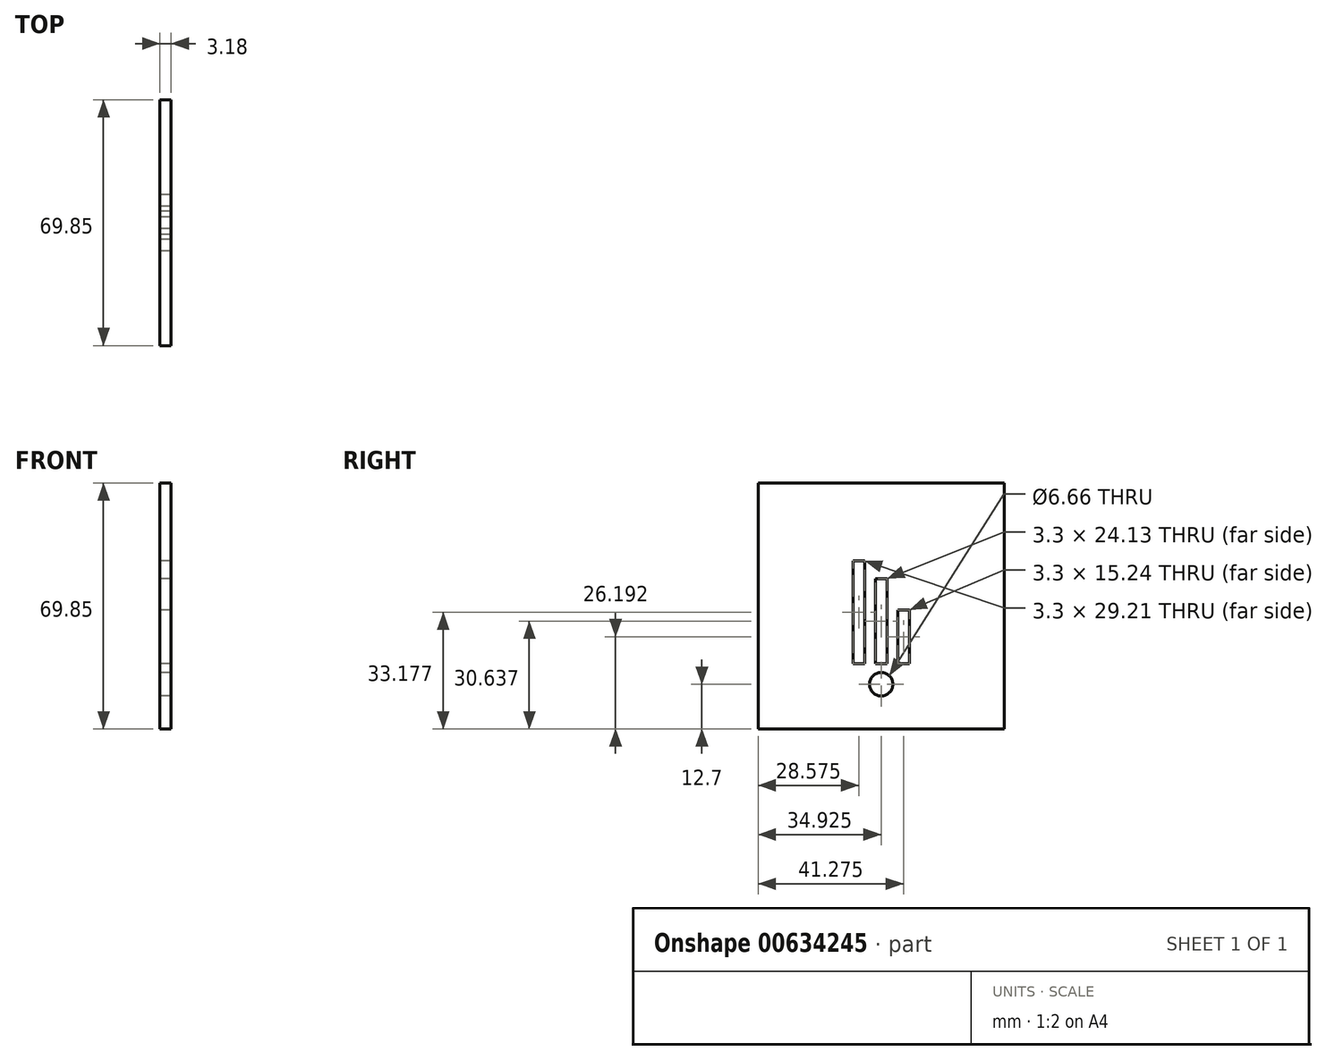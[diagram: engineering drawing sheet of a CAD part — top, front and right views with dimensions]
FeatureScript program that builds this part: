
annotation { "Feature Type Name" : "Feature", "Feature Type Description" : "" }
export const myFeature = defineFeature(function(context is Context, id is Id, definition is map)
    precondition{}
    {
        {
            var Q0;
            Q0=qCreatedBy(makeId("Right.planeOp"),FACE);
            var sketch = newSketch(context, id + "F0", { "sketchPlane" : qUnion([Q0])});
            skLineSegment(sketch, "E0.bottom", {"start": v(0, 0) * mm, "end": v(69.85, 0) * mm});
            skLineSegment(sketch, "E0.top", {"start": v(0, -69.85) * mm, "end": v(69.85, -69.85) * mm});
            skLineSegment(sketch, "E0.left", {"start": v(0, 0) * mm, "end": v(0, -69.85) * mm});
            skLineSegment(sketch, "E0.right", {"start": v(69.85, 0) * mm, "end": v(69.85, -69.85) * mm});
            skCircle(sketch, "E1", {"center": v(34.93, -57.15) * mm, "radius": 3.33 * mm});
            skLineSegment(sketch, "E2.bottom", {"start": v(26.92, -22.07) * mm, "end": v(30.23, -22.07) * mm});
            skLineSegment(sketch, "E2.top", {"start": v(26.92, -51.28) * mm, "end": v(30.23, -51.28) * mm});
            skLineSegment(sketch, "E2.left", {"start": v(26.92, -22.07) * mm, "end": v(26.92, -51.28) * mm});
            skLineSegment(sketch, "E2.right", {"start": v(30.23, -22.07) * mm, "end": v(30.23, -51.28) * mm});
            skLineSegment(sketch, "E3.bottom", {"start": v(33.27, -51.28) * mm, "end": v(36.58, -51.28) * mm});
            skLineSegment(sketch, "E3.top", {"start": v(33.27, -27.15) * mm, "end": v(36.58, -27.15) * mm});
            skLineSegment(sketch, "E3.left", {"start": v(33.27, -51.28) * mm, "end": v(33.27, -27.15) * mm});
            skLineSegment(sketch, "E3.right", {"start": v(36.58, -51.28) * mm, "end": v(36.58, -27.15) * mm});
            skLineSegment(sketch, "E4", {"start": v(0, -51.28) * mm, "end": v(69.85, -51.28) * mm, "construction": true});
            skLineSegment(sketch, "E5.bottom", {"start": v(42.93, -51.28) * mm, "end": v(39.62, -51.28) * mm});
            skLineSegment(sketch, "E5.top", {"start": v(42.93, -36.04) * mm, "end": v(39.62, -36.04) * mm});
            skLineSegment(sketch, "E5.left", {"start": v(42.93, -51.28) * mm, "end": v(42.93, -36.04) * mm});
            skLineSegment(sketch, "E5.right", {"start": v(39.62, -51.28) * mm, "end": v(39.62, -36.04) * mm});
            skLineSegment(sketch, "E6", {"start": v(34.93, -69.85) * mm, "end": v(34.93, 0) * mm, "construction": true});
            skPoint(sketch, "E7", {"position": v(34.93, -27.15) * mm});
            skSolve(sketch);
        }
        {
            var Q0;
            Q0 = qSketchRegion(id + "F0", true);
            extrude(context, id + "F1", {"entities" : qUnion([Q0]), "depth" : 3.17 * mm, "offsetDistance" : 25.4 * mm});
        }
    });
